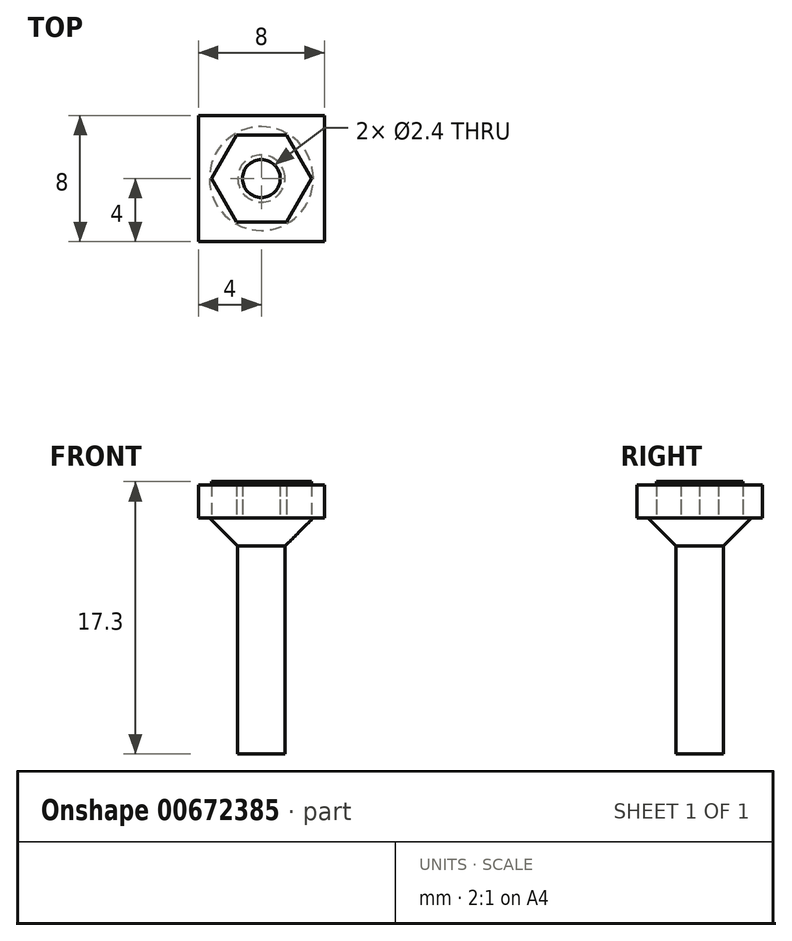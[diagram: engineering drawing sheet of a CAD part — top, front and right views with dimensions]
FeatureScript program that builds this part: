
annotation { "Feature Type Name" : "Feature", "Feature Type Description" : "" }
export const myFeature = defineFeature(function(context is Context, id is Id, definition is map)
    precondition{}
    {
        {
            var Q0;
            Q0=qCreatedBy(makeId("Top.planeOp"),FACE);
            var sketch = newSketch(context, id + "F0", { "sketchPlane" : qUnion([Q0])});
            skCircle(sketch, "E0", {"center": v(0, 0) * mm, "radius": 1.2 * mm});
            skCircle(sketch, "E1.cCircle", {"center": v(0, 0) * mm, "radius": 3.18 * mm, "construction": true});
            skLineSegment(sketch, "E1.0", {"start": v(1.59, 2.75) * mm, "end": v(3.18, 0) * mm});
            skLineSegment(sketch, "E1.1", {"start": v(3.18, 0) * mm, "end": v(1.59, -2.75) * mm});
            skLineSegment(sketch, "E1.2", {"start": v(1.59, -2.75) * mm, "end": v(-1.59, -2.75) * mm});
            skLineSegment(sketch, "E1.3", {"start": v(-1.59, -2.75) * mm, "end": v(-3.18, 0) * mm});
            skLineSegment(sketch, "E1.4", {"start": v(-3.18, 0) * mm, "end": v(-1.59, 2.75) * mm});
            skLineSegment(sketch, "E1.5", {"start": v(-1.59, 2.75) * mm, "end": v(1.59, 2.75) * mm});
            skSolve(sketch);
        }
        {
            var Q0;
            Q0 = qSketchRegion(id + "F0", true);
            extrude(context, id + "F1", {"entities" : qUnion([Q0]), "depth" : 2.3 * mm, "offsetDistance" : 25 * mm});
        }
        {
            var Q0;
            Q0=qCreatedBy(makeId("Top.planeOp"),FACE);
            var sketch = newSketch(context, id + "F2", { "sketchPlane" : qUnion([Q0])});
            skCircle(sketch, "E2", {"center": v(0, 0) * mm, "radius": 1.2 * mm});
            skLineSegment(sketch, "E3.bottom", {"start": v(4, -4) * mm, "end": v(-4, -4) * mm});
            skLineSegment(sketch, "E3.top", {"start": v(4, 4) * mm, "end": v(-4, 4) * mm});
            skLineSegment(sketch, "E3.left", {"start": v(4, -4) * mm, "end": v(4, 4) * mm});
            skLineSegment(sketch, "E3.right", {"start": v(-4, -4) * mm, "end": v(-4, 4) * mm});
            skSolve(sketch);
        }
        {
            var Q0;
            Q0 = qSketchRegion(id + "F2", true);
            extrude(context, id + "F3", {"entities" : qUnion([Q0]), "depth" : 2.1 * mm, "offsetDistance" : 25 * mm});
        }
        {
            var Q0;
            Q0=qCreatedBy(makeId("Front.planeOp"),FACE);
            var sketch = newSketch(context, id + "F4", { "sketchPlane" : qUnion([Q0])});
            skLineSegment(sketch, "E4", {"start": v(0, 0) * mm, "end": v(0, -15) * mm});
            skLineSegment(sketch, "E5", {"start": v(0, -15) * mm, "end": v(1.5, -15) * mm});
            skLineSegment(sketch, "E6", {"start": v(1.5, -15) * mm, "end": v(1.5, -1.8) * mm});
            skLineSegment(sketch, "E7", {"start": v(1.5, -1.8) * mm, "end": v(3.3, 0) * mm});
            skLineSegment(sketch, "E8", {"start": v(3.3, 0) * mm, "end": v(0, 0) * mm});
            skSolve(sketch);
        }
        {
            var Q0;
            Q0 = qSketchRegion(id + "F4", true);
            var Q1;
            Q1 = qConstructionFilter(qBodyType(qCreatedBy(id + "F4" ,EDGE), BodyType.WIRE), ConstructionObject.NO);
            var Q2;
            Q2=sQuery(id+"F4.wireOp",EDGE,"E4");
            revolve(context, id + "F5", {"surfaceOperationType" : NewSurfaceOperationType.NEW, "entities" : qUnion([Q0]), "surfaceEntities" : qUnion([Q1]), "axis" : qUnion([Q2]), "revolveType" : RevolveType.FULL});
        }
    });
